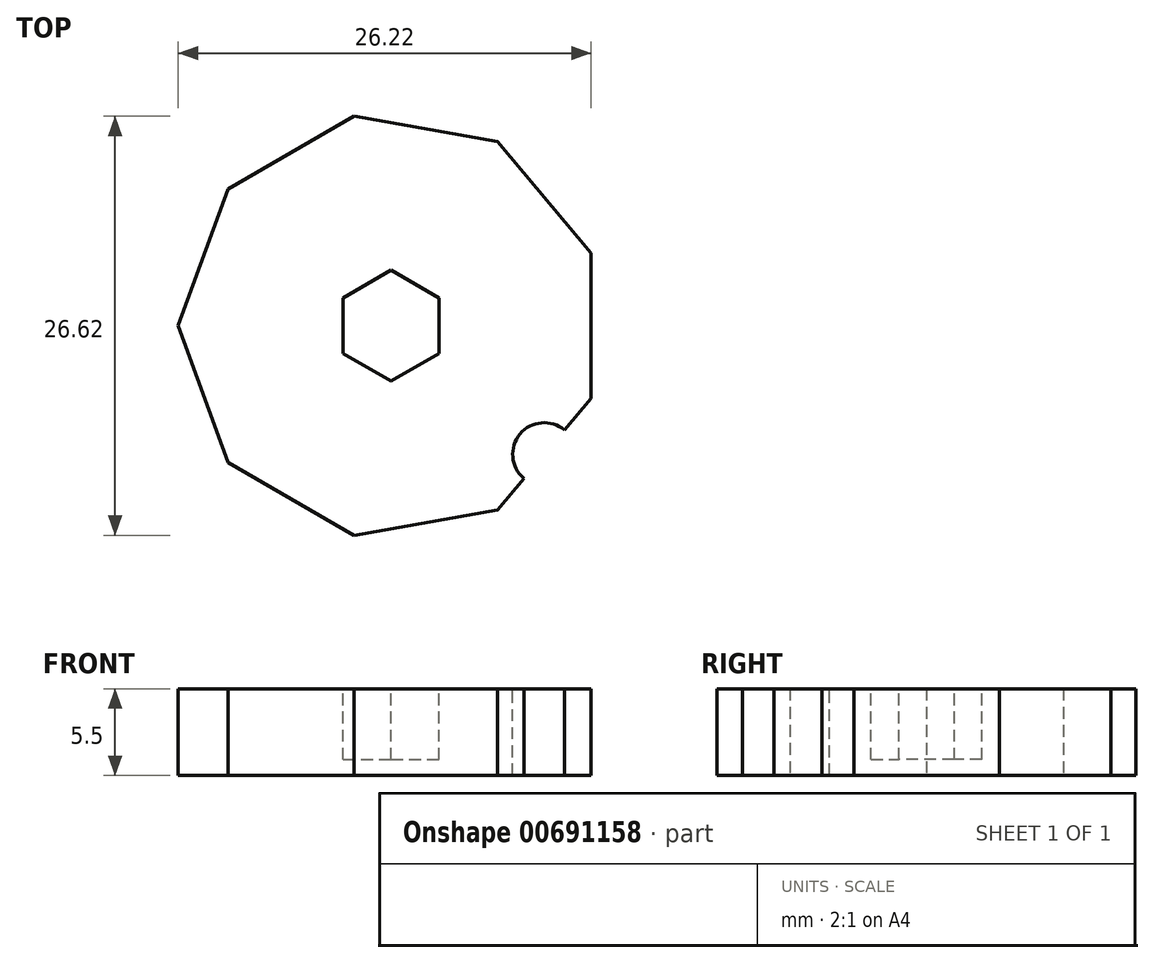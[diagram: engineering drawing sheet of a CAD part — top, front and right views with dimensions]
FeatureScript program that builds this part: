
annotation { "Feature Type Name" : "Feature", "Feature Type Description" : "" }
export const myFeature = defineFeature(function(context is Context, id is Id, definition is map)
    precondition{}
    {
        {
            var Q0;
            Q0=qCreatedBy(makeId("Top.planeOp"),FACE);
            var sketch = newSketch(context, id + "F0", { "sketchPlane" : qUnion([Q0])});
            skCircle(sketch, "E0.cCircle", {"center": v(0, 0) * mm, "radius": 12.7 * mm, "construction": true});
            skLineSegment(sketch, "E0.0", {"start": v(12.7, 4.62) * mm, "end": v(12.7, -4.62) * mm});
            skLineSegment(sketch, "E0.1", {"start": v(12.7, -4.62) * mm, "end": v(6.76, -11.7) * mm});
            skLineSegment(sketch, "E0.2", {"start": v(6.76, -11.7) * mm, "end": v(-2.35, -13.3) * mm});
            skLineSegment(sketch, "E0.3", {"start": v(-2.35, -13.3) * mm, "end": v(-10.35, -8.69) * mm});
            skLineSegment(sketch, "E0.4", {"start": v(-10.35, -8.69) * mm, "end": v(-13.52, 0) * mm});
            skLineSegment(sketch, "E0.5", {"start": v(-13.52, 0) * mm, "end": v(-10.35, 8.69) * mm});
            skLineSegment(sketch, "E0.6", {"start": v(-10.35, 8.69) * mm, "end": v(-2.35, 13.3) * mm});
            skLineSegment(sketch, "E0.7", {"start": v(-2.35, 13.3) * mm, "end": v(6.76, 11.7) * mm});
            skLineSegment(sketch, "E0.8", {"start": v(6.76, 11.7) * mm, "end": v(12.7, 4.62) * mm});
            skPoint(sketch, "E0.0.midPoint", {"position": v(12.7, 0) * mm});
            skSolve(sketch);
        }
        {
            var Q0;
            Q0=makeQuery(id+"F0.imprint","IMPRINT",FACE,{"disambiguationData":[TD([[makeQuery(id+"F0.imprint","IMPRINT",EDGE,{"derivedFrom":sQuery(id+"F0.wireOp",EDGE,"E0.0")}),-1.0]])]});
            extrude(context, id + "F1", {"entities" : qUnion([Q0]), "depth" : 5.5 * mm, "offsetDistance" : 25.4 * mm});
        }
        {
            var Q0;
            Q0=makeQuery(id+"F1.opExtrude","CAP_FACE",FACE,{"disambiguationData":[OSD([sQuery(id+"F0.wireOp",EDGE,"E0.0"),sQuery(id+"F0.wireOp",EDGE,"E0.1"),sQuery(id+"F0.wireOp",EDGE,"E0.2"),sQuery(id+"F0.wireOp",EDGE,"E0.3"),sQuery(id+"F0.wireOp",EDGE,"E0.4"),sQuery(id+"F0.wireOp",EDGE,"E0.5"),sQuery(id+"F0.wireOp",EDGE,"E0.6"),sQuery(id+"F0.wireOp",EDGE,"E0.7"),sQuery(id+"F0.wireOp",EDGE,"E0.8")])],"isStart":false});
            var sketch = newSketch(context, id + "F2", { "sketchPlane" : qUnion([Q0])});
            skCircle(sketch, "E1.cCircle", {"center": v(0, 0) * mm, "radius": 3.05 * mm, "construction": true});
            skLineSegment(sketch, "E1.0", {"start": v(3.05, 1.76) * mm, "end": v(3.05, -1.76) * mm});
            skLineSegment(sketch, "E1.1", {"start": v(3.05, -1.76) * mm, "end": v(0, -3.52) * mm});
            skLineSegment(sketch, "E1.2", {"start": v(0, -3.52) * mm, "end": v(-3.05, -1.76) * mm});
            skLineSegment(sketch, "E1.3", {"start": v(-3.05, -1.76) * mm, "end": v(-3.05, 1.76) * mm});
            skLineSegment(sketch, "E1.4", {"start": v(-3.05, 1.76) * mm, "end": v(0, 3.52) * mm});
            skLineSegment(sketch, "E1.5", {"start": v(0, 3.52) * mm, "end": v(3.05, 1.76) * mm});
            skPoint(sketch, "E1.0.midPoint", {"position": v(3.05, 0) * mm});
            skSolve(sketch);
        }
        {
            var Q0;
            Q0=makeQuery(id+"F2.imprint","IMPRINT",FACE,{"disambiguationData":[TD([[makeQuery(id+"F2.imprint","IMPRINT",EDGE,{"derivedFrom":sQuery(id+"F2.wireOp",EDGE,"E1.0")}),-1.0]])]});
            extrude(context, id + "F3", {"entities" : qUnion([Q0]), "operationType" : NewBodyOperationType.REMOVE, "oppositeDirection" : true, "depth" : 4.5 * mm, "offsetDistance" : 25.4 * mm});
        }
        {
            var Q0;
            Q0=makeQuery(id+"F1.opExtrude","CAP_FACE",FACE,{"disambiguationData":[OSD([sQuery(id+"F0.wireOp",EDGE,"E0.0"),sQuery(id+"F0.wireOp",EDGE,"E0.1"),sQuery(id+"F0.wireOp",EDGE,"E0.2"),sQuery(id+"F0.wireOp",EDGE,"E0.3"),sQuery(id+"F0.wireOp",EDGE,"E0.4"),sQuery(id+"F0.wireOp",EDGE,"E0.5"),sQuery(id+"F0.wireOp",EDGE,"E0.6"),sQuery(id+"F0.wireOp",EDGE,"E0.7"),sQuery(id+"F0.wireOp",EDGE,"E0.8")])],"isStart":false});
            var sketch = newSketch(context, id + "F4", { "sketchPlane" : qUnion([Q0])});
            skCircle(sketch, "E2", {"center": v(9.73, -8.16) * mm, "radius": 2 * mm});
            skSolve(sketch);
        }
        {
            var Q0;
            {var subQ0=sQuery(id+"F4.wireOp",EDGE,"E2");var subQ1=makeQuery(id+"F1.opExtrude","CAP_EDGE",EDGE,{"disambiguationData":[OSD([sQuery(id+"F0.wireOp",EDGE,"E0.1")])],"isStart":false});var subQ2=makeQuery(id+"F4.imprint","INTERSECT",VERTEX,{"disambiguationData":[OD(0.0)],"derivedFrom":[subQ1,subQ0]});Q0=makeQuery(id+"F4.imprint","IMPRINT",FACE,{"disambiguationData":[TD([[makeQuery(id+"F4.imprint","IMPRINT",EDGE,{"disambiguationData":[TD([[subQ2,-1.0]])],"derivedFrom":subQ0}),1.0]])]});}
            extrude(context, id + "F5", {"entities" : qUnion([Q0]), "operationType" : NewBodyOperationType.REMOVE, "oppositeDirection" : true, "depth" : 25.4 * mm, "offsetDistance" : 25.4 * mm});
        }
    });
